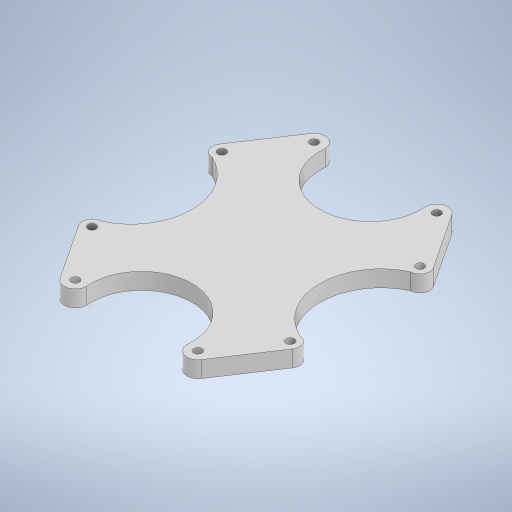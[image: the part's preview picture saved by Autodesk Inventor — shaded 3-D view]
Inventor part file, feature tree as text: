
AUTODESK INVENTOR PART (.ipt)
format: ipt  version: 2023 (Build 270158000, 158)  size: 309,248 bytes
history: native  units: in
note: dims shown in document units (in); Inventor stores cm internally (conversion verified against a paired STEP export)
features: sketch x2, plane x1, extrude x1
ambient origin geometry x8: Origin, YZ Plane, XZ Plane, XY Plane, X Axis, Y Axis, Z Axis, Center Point
bodies: Body1 (feature_tree)
feature tree (4):
  sketch  "Sketch1"  dims[d2=2.1654in d10=0.315in]
  plane  "Work Plane1"
  extrude  "Extrusion1"  Depth=0.315in
  sketch  "Sketch6"  dims[d11=0.315in d12=0.315in d13=0.315in d14=0.2756in d15=0.2756in d16=0.2756in d17=0.2756in d18=0.2362in d19=0.0in d5=0.0197in d6=0.0344in d7=0.0197in d8=0.0344in d20=0.0in d21=0.0in d22=0.0in d23=0.0in d24=0.0in d25=0.0in]
